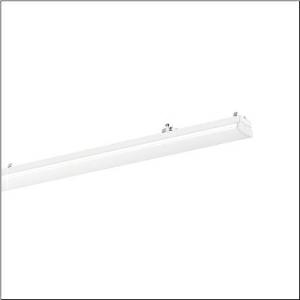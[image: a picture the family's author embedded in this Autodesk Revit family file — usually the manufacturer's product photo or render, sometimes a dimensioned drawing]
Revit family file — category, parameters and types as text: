
# Revit family: licross_21_recessed_opal_mo_52te1dvn445g
name_source: partatom
category: Lighting Fixtures
units: mm (PartAtom-declared; Revit-internal decimal feet)

## family parameters
Cut with Voids When Loaded = No
Host = Face
Light Source = No
Part Type = Normal
Room Calculation Point = No
Round Connector Dimension = Use Diameter
Shared = No

## types (1)
- --- (1 x LED, 4500 lm, 25.8 W, 4000K)
    Apparent Load = 26 VA
    CIE Flux Codes = 44 73 91 87 100
    Color Rendering = 80
    Color Temperature = 4000K
    Default Elevation = 1800 mm
    Description = Licross 21 recessed opal MO, luminaire insert, of sheet steel, galvanised, coil coated, white, length: 1.500mm, width: 66mm, height: 67mm, LED rated luminous flux: 4.500lm, light colour: 840, SDCM (Standard Deviation of Colour Matching)MacAdam ≤ 3 SDCM (initial), control gear: DALI 2, CLO, with plug, 5-pole, with phase selection, mains connection: 220..240V, AC, 50/60Hz, start of lifetime: 26W, end of service life: 30W, internal wiring halogen-free, primary optical cover: cover, of PMMA, light emission: direct with ceiling illumination distribution, primary light characteristic: symmetric, protection rating (complete): IP54, insulation class (complete): insulation class I (protective earthing), certification: CE, ENEC, VDE, UKCA, protection symbol: D if used in an environment with non-conductive dust loads with corresponding accessories, impact resistance: IK06, permissible ambient temperature for indoor applications: -25..+45°C, corresponds to IFS (International Featured Standards) requirements for safety and quality in the food industry, reducing of maximum allowable ambient temperature of 5°C with ceiling mounting, LABS conformity tested according to VDMA 24364:2018-05, The light source and the operating device comply with the requirements of the Ecodesign Regulation (EU) 2019/2020 and are replaceable in accordance with this regulation, packaging unit: 1 piece
    Height = 83 mm
    Lamp = 1 x LED
    Lamp Light Flux = 4500 lm
    Lamp Power = 25.8 W
    Lamp count = 1
    Length = 1500 mm
    Luminous efficacy = 174 lm/W
    Manufacturer = Siteco
    ModVariant = No
    Model = 52TE1DVN445G
    Mounting Place = Ceiling
    Mounting Type = Pendant
    Number of Poles = 1
    OnlyDefault = Yes
    Power Factor = 1
    Product Name = Licross 21 recessed opal MO
    Product group = luminaire insert | ceiling pendant
    ProductGroupID = 901
    Protection Class = Protection class I
    Protection Degree = IP 54
    RLX_Detail_Level = 1
    RLX_Emergency_Light_Flux = 0 lm
    RLX_Emergency_Type = 0
    RLX_Emergency_Type_DB = No
    RlxData = <blob elided: 26585 chars, md5=d4eccd53>
    Socket = socket
    Standby Power = 0 W
    System Light Flux = 4500 lm
    System Power = 26 W
    Type Comments = factory setting: luminous flux: 100 % | dim-lin: 254 | 172 mA
    Type Image = l_1313666.jpg
    URL = http://relux.com
    VarID = @adj_076007
    Voltage = 0 V
    Weight = 0.00 kg
    Width = 76 mm

## geometry (parser evidence)
native form markers: Blend x4, Sweep x13
no freeform markers — native parametric forms only
